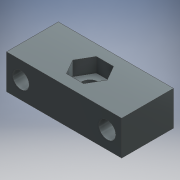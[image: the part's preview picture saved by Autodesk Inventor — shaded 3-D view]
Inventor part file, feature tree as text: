
AUTODESK INVENTOR PART (.ipt)
format: ipt  version: 2016 (Build 200138000, 138)  size: 144,384 bytes
history: native  units: mm
features: extrude x3, sketch x3
ambient origin geometry x8: Origin, YZ Plane, XZ Plane, XY Plane, X Axis, Y Axis, Z Axis, Center Point
bodies: Solid1 (feature_tree)
feature tree (6):
  extrude  "Extrusion1"  Depth=12.0mm
  extrude  "Extrusion8"  Depth=5.9mm
  extrude  "Extrusion9"  Depth=5.0mm
  sketch  "Sketch1"  dims[d0=40.0mm d1=12.0mm]
  sketch  "Sketch8"  dims[d2=5.7mm d3=5.9mm]
  sketch  "Sketch9"  dims[d4=5.0mm d6=6.0mm d7=18.0mm d8=0.0mm d33=5.0mm d34=5.9mm d35=20.0mm d36=9.0mm d37=5.0mm d38=0.0mm d39=10.4mm d40=5.0mm d41=0.0mm]
